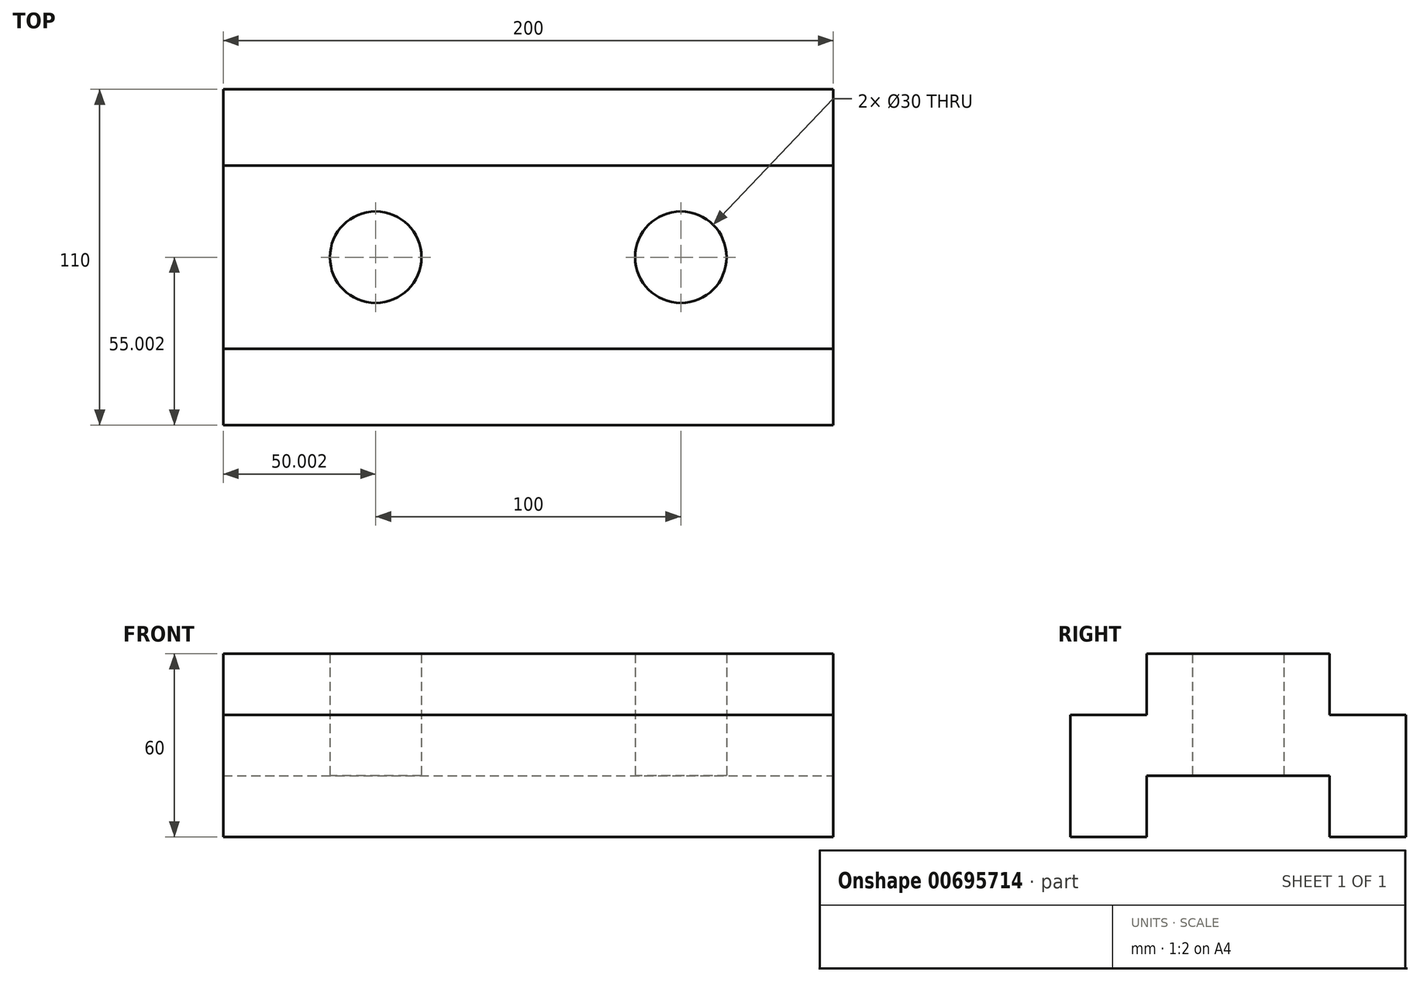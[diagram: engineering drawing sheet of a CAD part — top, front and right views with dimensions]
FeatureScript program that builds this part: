
annotation { "Feature Type Name" : "Feature", "Feature Type Description" : "" }
export const myFeature = defineFeature(function(context is Context, id is Id, definition is map)
    precondition{}
    {
        {
            var Q0;
            Q0=qCreatedBy(makeId("Top.planeOp"),FACE);
            var sketch = newSketch(context, id + "F0", { "sketchPlane" : qUnion([Q0])});
            skLineSegment(sketch, "E0", {"start": v(-97.7, 25.03) * mm, "end": v(102.3, 25.03) * mm});
            skLineSegment(sketch, "E1", {"start": v(-97.7, 25.03) * mm, "end": v(-97.7, -34.97) * mm});
            skLineSegment(sketch, "E2", {"start": v(-97.7, -34.97) * mm, "end": v(102.3, -34.97) * mm});
            skLineSegment(sketch, "E3", {"start": v(102.3, -34.97) * mm, "end": v(102.3, 25.03) * mm});
            skCircle(sketch, "E4", {"center": v(-47.7, -4.97) * mm, "radius": 15 * mm});
            skCircle(sketch, "E5", {"center": v(52.3, -4.97) * mm, "radius": 15 * mm});
            skPoint(sketch, "E6.start.orphan", {"position": v(-47.7, 25.03) * mm});
            skPoint(sketch, "E7.trimOffspring.end.orphan", {"position": v(-47.7, -34.97) * mm});
            skPoint(sketch, "E8.start.orphan", {"position": v(-97.7, -4.97) * mm});
            skPoint(sketch, "E9.trimOffspring.end.orphan", {"position": v(102.3, -4.97) * mm});
            skPoint(sketch, "E10.trimOffspring.end.orphan", {"position": v(52.3, -34.97) * mm});
            skPoint(sketch, "E11.start.orphan", {"position": v(52.3, 25.03) * mm});
            skSolve(sketch);
        }
        {
            var Q0;
            Q0 = qSketchRegion(id + "F0", true);
            extrude(context, id + "F1", {"entities" : qUnion([Q0]), "depth" : 40 * mm, "offsetDistance" : 25 * mm});
        }
        {
            var Q0;
            Q0=makeQuery(id+"F1.opExtrude","SWEPT_FACE",FACE,{"disambiguationData":[OSD([sQuery(id+"F0.wireOp",EDGE,"E2")])]});
            var sketch = newSketch(context, id + "F2", { "sketchPlane" : qUnion([Q0])});
            skLineSegment(sketch, "E12", {"start": v(102.3, 20) * mm, "end": v(-97.7, 20) * mm});
            skLineSegment(sketch, "E13", {"start": v(-97.7, 20) * mm, "end": v(-97.7, -20) * mm});
            skLineSegment(sketch, "E14", {"start": v(-97.7, -20) * mm, "end": v(102.3, -20) * mm});
            skLineSegment(sketch, "E15", {"start": v(102.3, -20) * mm, "end": v(102.3, 20) * mm});
            skSolve(sketch);
        }
        {
            var Q0;
            Q0 = qSketchRegion(id + "F2", true);
            extrude(context, id + "F3", {"entities" : qUnion([Q0]), "operationType" : NewBodyOperationType.ADD, "depth" : 25 * mm, "offsetDistance" : 25 * mm});
        }
        {
            var Q0;
            Q0=makeQuery(id+"F1.opExtrude","SWEPT_FACE",FACE,{"disambiguationData":[OSD([sQuery(id+"F0.wireOp",EDGE,"E0")])]});
            var sketch = newSketch(context, id + "F4", { "sketchPlane" : qUnion([Q0])});
            skLineSegment(sketch, "E16", {"start": v(-102.3, 20) * mm, "end": v(-102.3, -20) * mm});
            skLineSegment(sketch, "E17", {"start": v(-102.3, 20) * mm, "end": v(97.7, 20) * mm});
            skLineSegment(sketch, "E18", {"start": v(97.7, 20) * mm, "end": v(97.7, -20) * mm});
            skLineSegment(sketch, "E19", {"start": v(97.7, -20) * mm, "end": v(-102.3, -20) * mm});
            skSolve(sketch);
        }
        {
            var Q0;
            Q0 = qSketchRegion(id + "F4", true);
            extrude(context, id + "F5", {"entities" : qUnion([Q0]), "operationType" : NewBodyOperationType.ADD, "depth" : 25 * mm, "offsetDistance" : 25 * mm});
        }
    });
